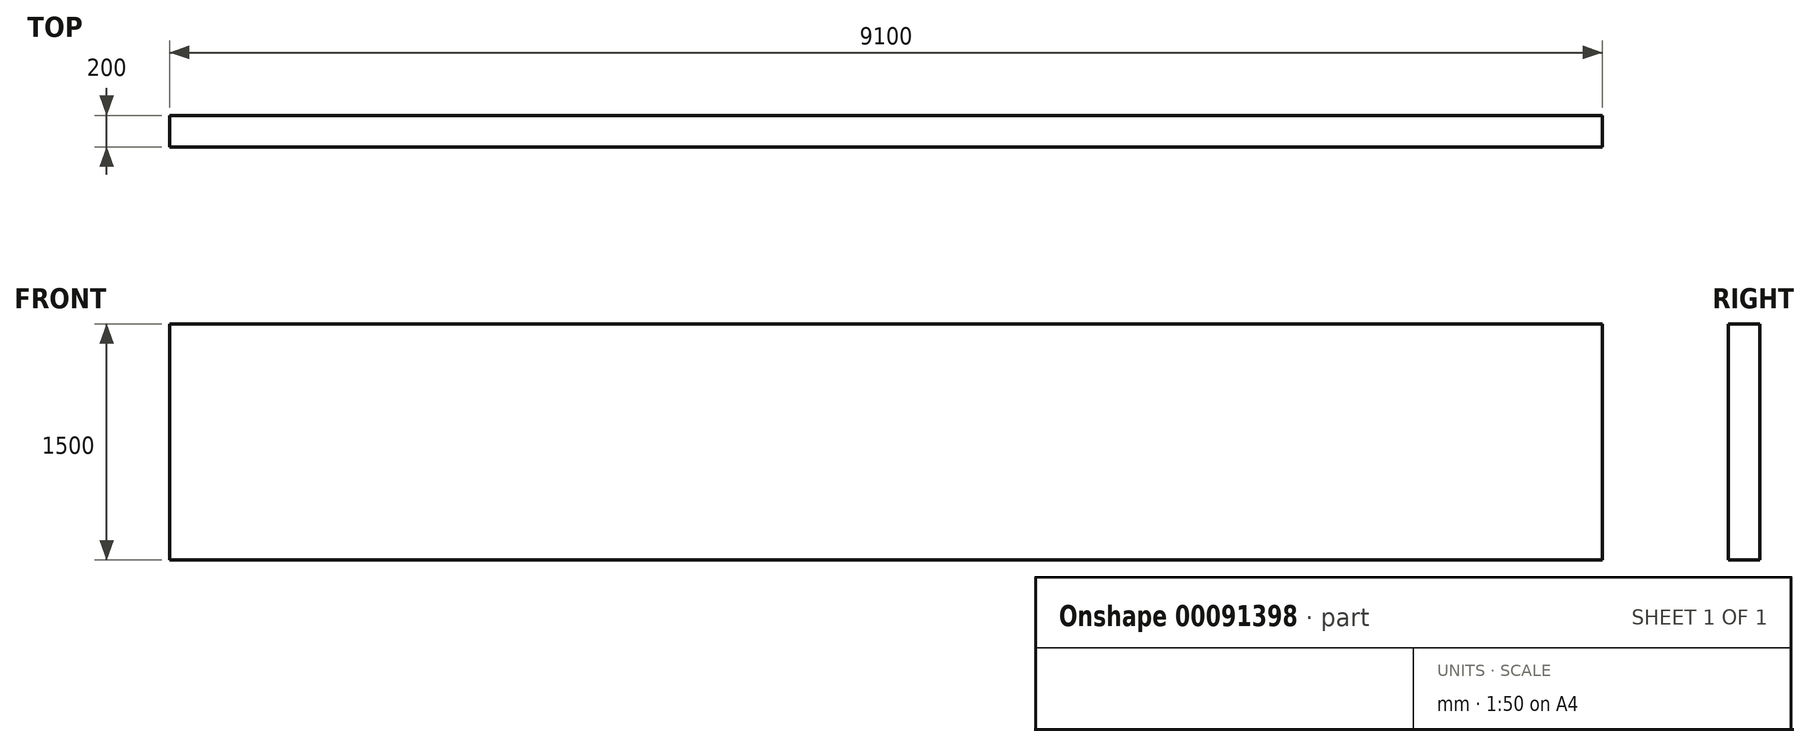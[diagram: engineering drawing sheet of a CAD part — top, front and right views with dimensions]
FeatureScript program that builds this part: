
annotation { "Feature Type Name" : "Feature", "Feature Type Description" : "" }
export const myFeature = defineFeature(function(context is Context, id is Id, definition is map)
    precondition{}
    {
        {
            var Q0;
            Q0=qCreatedBy(makeId("Front.planeOp"),FACE);
            var sketch = newSketch(context, id + "F0", { "sketchPlane" : qUnion([Q0])});
            skLineSegment(sketch, "E0.bottom", {"start": v(-3284.26, 753.24) * mm, "end": v(5815.74, 753.24) * mm});
            skLineSegment(sketch, "E0.top", {"start": v(-3284.26, -746.76) * mm, "end": v(5815.74, -746.76) * mm});
            skLineSegment(sketch, "E0.left", {"start": v(-3284.26, 753.24) * mm, "end": v(-3284.26, -746.76) * mm});
            skLineSegment(sketch, "E0.right", {"start": v(5815.74, 753.24) * mm, "end": v(5815.74, -746.76) * mm});
            skSolve(sketch);
        }
        {
            var Q0;
            Q0=qSketchRegion(id+"F0",true);
            extrude(context, id + "F1", {"entities" : qUnion([Q0]), "depth" : 200 * mm});
        }
    });
